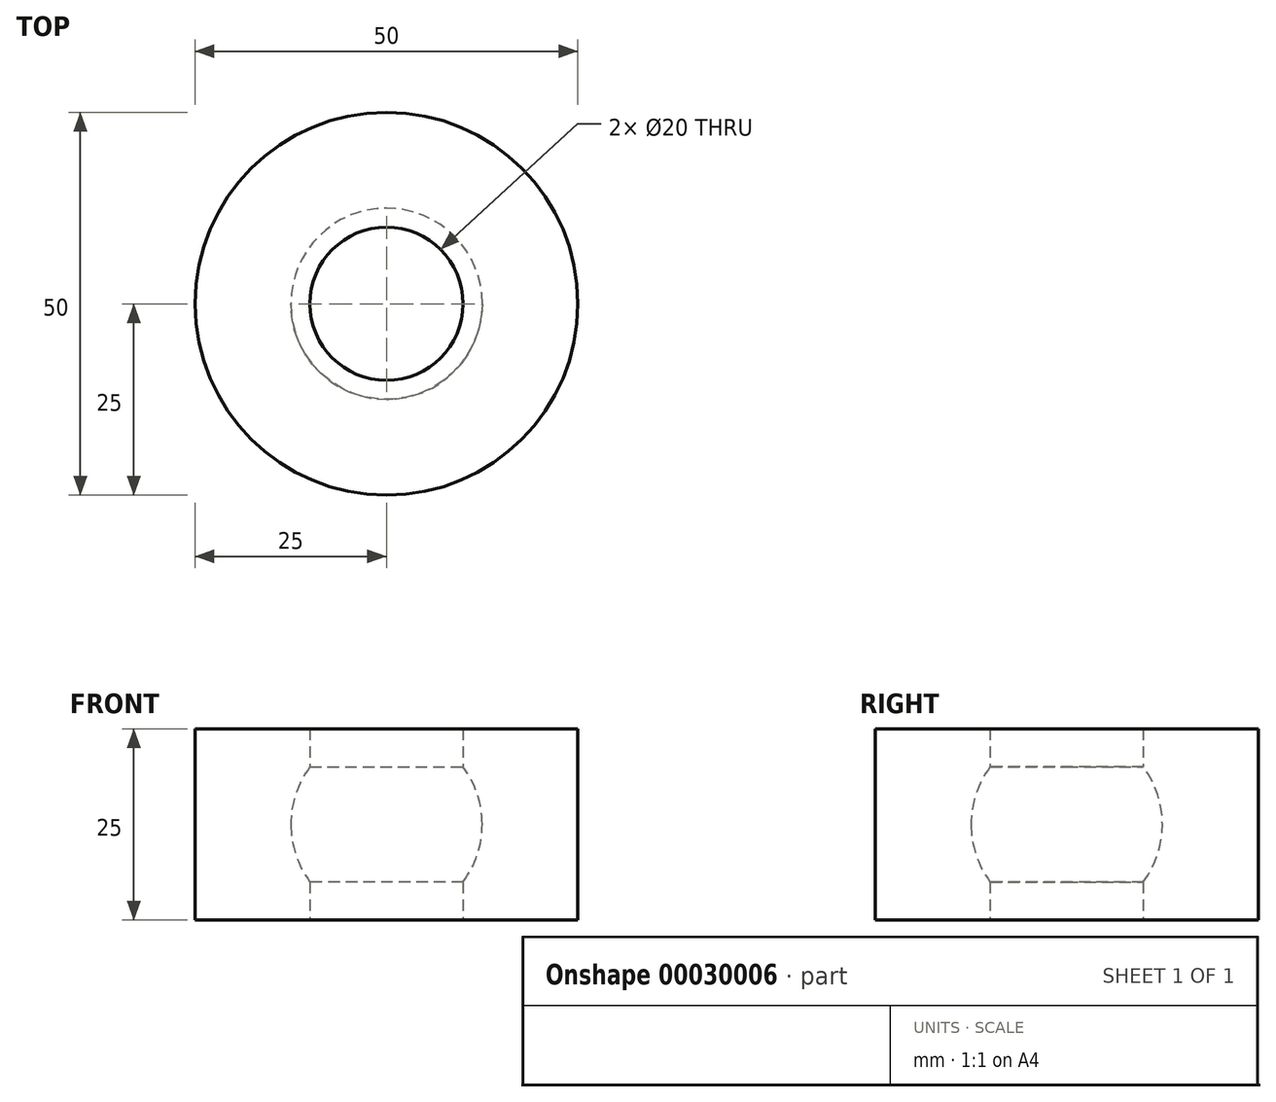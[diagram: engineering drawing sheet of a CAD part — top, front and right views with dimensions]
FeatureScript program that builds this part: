
annotation { "Feature Type Name" : "Feature", "Feature Type Description" : "" }
export const myFeature = defineFeature(function(context is Context, id is Id, definition is map)
    precondition{}
    {
        {
            var Q0;
            Q0=qCreatedBy(makeId("Top.planeOp"),FACE);
            var sketch = newSketch(context, id + "F0", { "sketchPlane" : qUnion([Q0])});
            skCircle(sketch, "E0", {"center": v(0, 0) * mm, "radius": 25 * mm});
            skCircle(sketch, "E1", {"center": v(0, 0) * mm, "radius": 10 * mm});
            skSolve(sketch);
        }
        {
            var Q0;
            Q0=makeQuery(id+"F0.imprint","IMPRINT",FACE,{"disambiguationData":[TD([[makeQuery(id+"F0.imprint","IMPRINT",EDGE,{"derivedFrom":sQuery(id+"F0.wireOp",EDGE,"E0")}),1.0]])]});
            extrude(context, id + "F1", {"entities" : qUnion([Q0]), "endBound" : BoundingType.SYMMETRIC, "depth" : 25 * mm, "hasSecondDirection" : true, "secondDirectionOppositeDirection" : true, "secondDirectionDepth" : 25 * mm});
        }
        {
            var Q0;
            Q0=qCreatedBy(makeId("Top.planeOp"),FACE);
            var sketch = newSketch(context, id + "F2", { "sketchPlane" : qUnion([Q0])});
            skArc(sketch, "E2", {"start": v(-12.5, 0) * mm, "mid": v(0, -12.5) * mm, "end": v(12.5, 0) * mm});
            skLineSegment(sketch, "E3", {"start": v(50.8, 0) * mm, "end": v(-50.4, 0) * mm});
            skSolve(sketch);
        }
        {
            var Q0;
            {var subQ1=sQuery(id+"F2.wireOp",EDGE,"E2");Q0=makeQuery(id+"F2.imprint","IMPRINT",FACE,{"disambiguationData":[TD([[makeQuery(id+"F2.imprint","IMPRINT",EDGE,{"derivedFrom":subQ1}),1.0]])]});}
            var Q1;
            Q1=sQuery(id+"F2.wireOp",EDGE,"E3");
            revolve(context, id + "F3", {"operationType" : NewBodyOperationType.REMOVE, "entities" : qUnion([Q0]), "axis" : qUnion([Q1]), "revolveType" : RevolveType.FULL, "oppositeDirection" : true});
        }
    });
